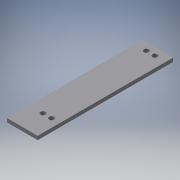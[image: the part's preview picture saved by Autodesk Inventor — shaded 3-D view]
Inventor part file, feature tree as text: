
AUTODESK INVENTOR PART (.ipt)
format: ipt  version: 2016 (Build 200138000, 138)  size: 103,424 bytes
history: native  units: mm
features: reference x6, extrude x3, sketch x3
ambient origin geometry x8: Origin, YZ Plane, XZ Plane, XY Plane, X Axis, Y Axis, Z Axis, Center Point
bodies: Solid1 (feature_tree)
feature tree (12):
  extrude  "Extrusion1"  Depth=220.0mm
  extrude  "Extrusion2"  TaperAngle=0.0deg  [1 undecoded]
  extrude  "Extrusion3"  [1 undecoded]
  sketch  "Sketch1"  dims[d0=50.0mm d1=220.0mm]
  sketch  "Sketch2"  dims[d2=6.0mm d3=0.0mm d4=0.0mm d5=0.0mm]
  reference  "Reference1"
  reference  "Reference2"
  reference  "Reference3"
  reference  "Reference4"
  sketch  "Sketch3"  dims[d6=6.0mm d7=0.0mm]
  reference  "Reference5"
  reference  "Reference6"
note: 2 required parameter values undecoded (feature->parameter linkage not recoverable at this tier; creation-order binding heuristic only, values carry confidence <= 0.55)
